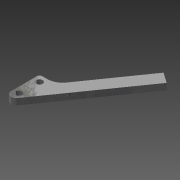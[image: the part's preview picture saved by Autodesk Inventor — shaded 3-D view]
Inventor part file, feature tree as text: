
AUTODESK INVENTOR PART (.ipt)
format: ipt  version: 2015 (Build 190159000, 159)  size: 108,544 bytes
history: native  units: mm
features: other x3, fillet x3, sketch x2, hole x1
ambient origin geometry x8: Origin, YZ Plane, XZ Plane, XY Plane, X Axis, Y Axis, Z Axis, Center Point
bodies: Body1 (feature_tree)
feature tree (9):
  other  "Bryła1"
  other  "Powierzchnia1"
  hole  "Otwór1"  [1 undecoded]
  fillet  "Zaokrąglenie2"  Radius=35.0mm
  fillet  "Zaokrąglenie3"  Radius=50.0mm
  fillet  "Zaokrąglenie4"  Radius=25.0mm
  sketch  "Szkic1"
  other  "Płyta1"
  sketch  "Szkic2"
note: 1 required parameter value undecoded (feature->parameter linkage not recoverable at this tier; creation-order binding heuristic only, values carry confidence <= 0.55)
